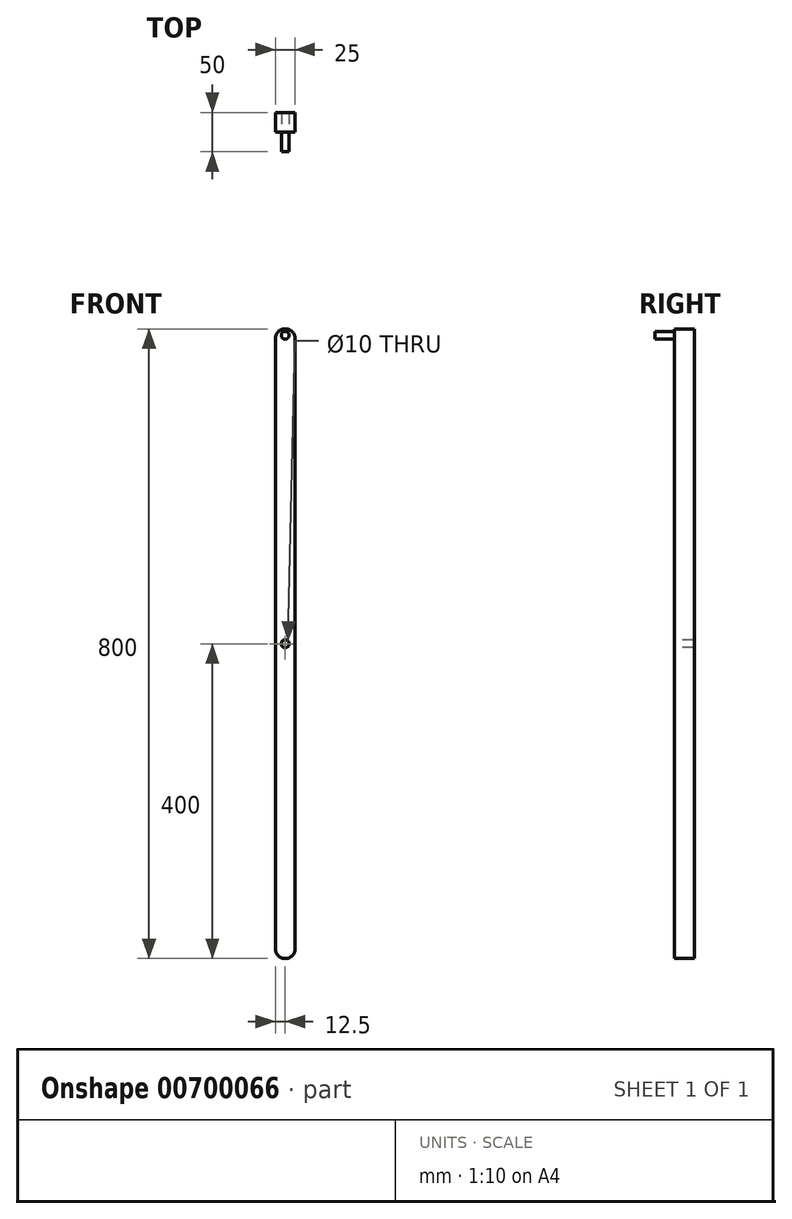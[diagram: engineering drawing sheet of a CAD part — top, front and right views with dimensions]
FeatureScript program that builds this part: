
annotation { "Feature Type Name" : "Feature", "Feature Type Description" : "" }
export const myFeature = defineFeature(function(context is Context, id is Id, definition is map)
    precondition{}
    {
        {
            var Q0;
            Q0=qCreatedBy(makeId("Front.planeOp"),FACE);
            var sketch = newSketch(context, id + "F0", { "sketchPlane" : qUnion([Q0])});
            skLineSegment(sketch, "E0.bottom", {"start": v(12.5, 400) * mm, "end": v(-12.5, 400) * mm});
            skLineSegment(sketch, "E0.top", {"start": v(12.5, -400) * mm, "end": v(-12.5, -400) * mm});
            skLineSegment(sketch, "E0.left", {"start": v(12.5, 400) * mm, "end": v(12.5, -400) * mm});
            skLineSegment(sketch, "E0.right", {"start": v(-12.5, 400) * mm, "end": v(-12.5, -400) * mm});
            skPoint(sketch, "E0.middle", {"position": v(0, 0) * mm});
            skSolve(sketch);
        }
        {
            var Q0;
            Q0 = qSketchRegion(id + "F0", true);
            extrude(context, id + "F1", {"entities" : qUnion([Q0]), "depth" : 25 * mm, "offsetDistance" : 25 * mm});
        }
        {
            var Q0;
            Q0=makeQuery(id+"F1.opExtrude","CAP_FACE",FACE,{"disambiguationData":[OSD([sQuery(id+"F0.wireOp",EDGE,"E0.bottom"),sQuery(id+"F0.wireOp",EDGE,"E0.top"),sQuery(id+"F0.wireOp",EDGE,"E0.left"),sQuery(id+"F0.wireOp",EDGE,"E0.right")])],"isStart":false});
            var sketch = newSketch(context, id + "F2", { "sketchPlane" : qUnion([Q0])});
            skCircle(sketch, "E1", {"center": v(0, 391.86) * mm, "radius": 5 * mm});
            skSolve(sketch);
        }
        {
            var Q0;
            Q0 = qSketchRegion(id + "F2", true);
            extrude(context, id + "F3", {"entities" : qUnion([Q0]), "operationType" : NewBodyOperationType.ADD, "depth" : 25 * mm, "offsetDistance" : 25 * mm});
        }
        {
            var Q0;
            Q0=makeQuery(id+"F1.opExtrude","CAP_FACE",FACE,{"disambiguationData":[OSD([sQuery(id+"F0.wireOp",EDGE,"E0.bottom"),sQuery(id+"F0.wireOp",EDGE,"E0.top"),sQuery(id+"F0.wireOp",EDGE,"E0.left"),sQuery(id+"F0.wireOp",EDGE,"E0.right")])],"isStart":false});
            var sketch = newSketch(context, id + "F4", { "sketchPlane" : qUnion([Q0])});
            skCircle(sketch, "E2", {"center": v(0, 0) * mm, "radius": 5 * mm});
            skSolve(sketch);
        }
        {
            var Q0;
            Q0=makeQuery(id+"F4.imprint","IMPRINT",FACE,{"disambiguationData":[TD([[makeQuery(id+"F4.imprint","IMPRINT",EDGE,{"derivedFrom":sQuery(id+"F4.wireOp",EDGE,"E2")}),1.0]])]});
            extrude(context, id + "F5", {"entities" : qUnion([Q0]), "operationType" : NewBodyOperationType.REMOVE, "oppositeDirection" : true, "depth" : 25 * mm, "offsetDistance" : 25 * mm});
        }
        {
            var Q0;
            Q0=makeQuery(id+"F1.opExtrude","SWEPT_EDGE",EDGE,{"disambiguationData":[OSD([sQuery(id+"F0.wireOp",EDGE,"E0.bottom"),sQuery(id+"F0.wireOp",EDGE,"E0.right")])]});
            var Q1;
            Q1=makeQuery(id+"F1.opExtrude","SWEPT_EDGE",EDGE,{"disambiguationData":[OSD([sQuery(id+"F0.wireOp",EDGE,"E0.bottom"),sQuery(id+"F0.wireOp",EDGE,"E0.left")])]});
            fillet(context, id + "F6", {"entities" : qUnion([Q0, Q1]), "radius" : 12.5 * mm, "tangentPropagation" : true, "allowEdgeOverflow" : false});
        }
        {
            var Q0;
            Q0=makeQuery(id+"F1.opExtrude","SWEPT_EDGE",EDGE,{"disambiguationData":[OSD([sQuery(id+"F0.wireOp",EDGE,"E0.top"),sQuery(id+"F0.wireOp",EDGE,"E0.left")])]});
            var Q1;
            Q1=makeQuery(id+"F1.opExtrude","SWEPT_EDGE",EDGE,{"disambiguationData":[OSD([sQuery(id+"F0.wireOp",EDGE,"E0.top"),sQuery(id+"F0.wireOp",EDGE,"E0.right")])]});
            fillet(context, id + "F7", {"entities" : qUnion([Q0, Q1]), "radius" : 12.5 * mm, "tangentPropagation" : true, "allowEdgeOverflow" : false});
        }
    });
